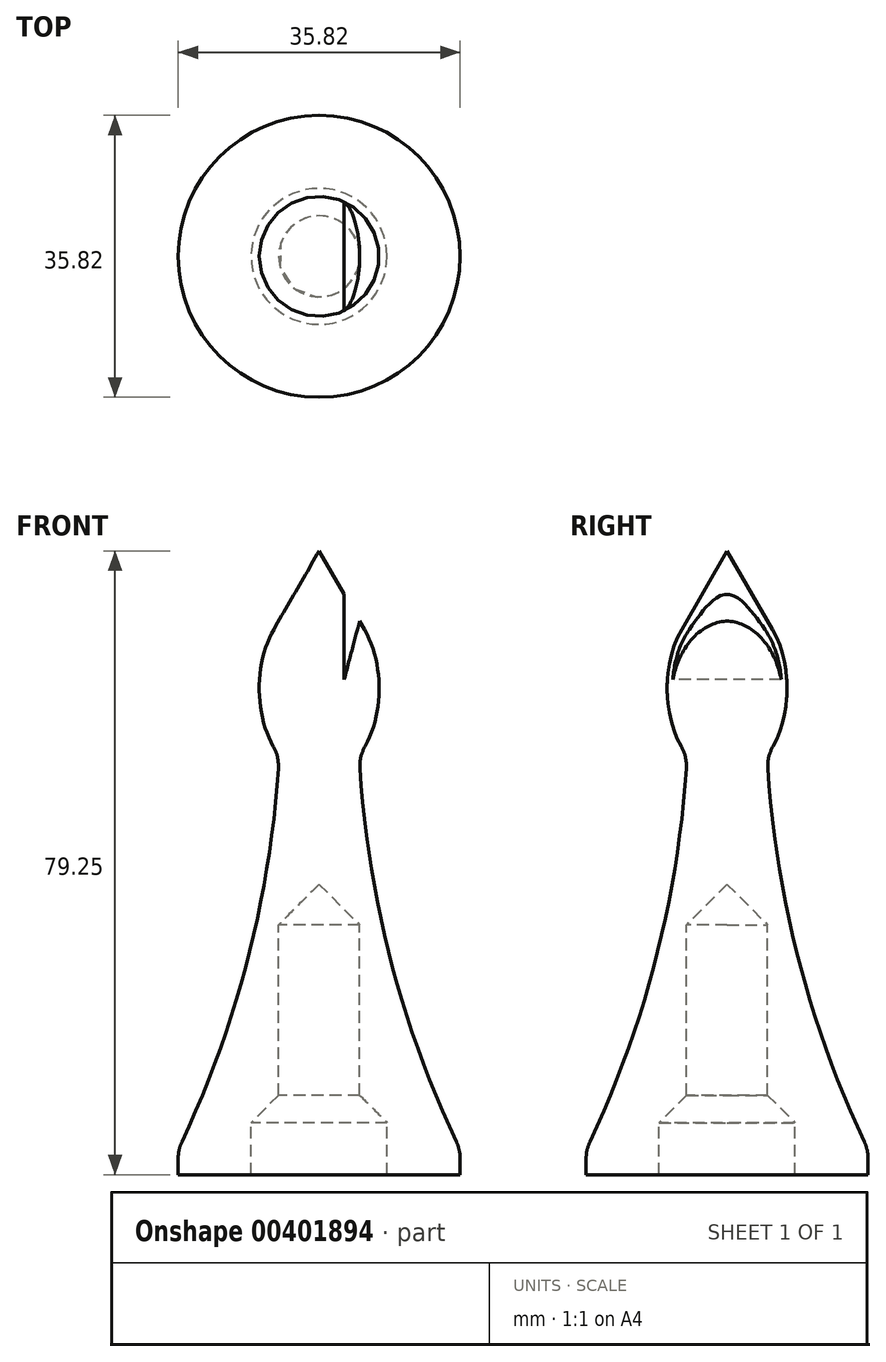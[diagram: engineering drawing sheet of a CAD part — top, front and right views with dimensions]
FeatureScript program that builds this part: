
annotation { "Feature Type Name" : "Feature", "Feature Type Description" : "" }
export const myFeature = defineFeature(function(context is Context, id is Id, definition is map)
    precondition{}
    {
        {
            var Q0;
            Q0=qCreatedBy(makeId("Front.planeOp"),FACE);
            var sketch = newSketch(context, id + "F0", { "sketchPlane" : qUnion([Q0])});
            skLineSegment(sketch, "E0", {"start": v(0, 0) * mm, "end": v(-8.64, 0) * mm, "construction": true});
            skLineSegment(sketch, "E1", {"start": v(-17.9, 0) * mm, "end": v(-17.9, 3.17) * mm});
            skArc(sketch, "E2", {"start": v(-17.9, 3.17) * mm, "mid": v(-9, 27.62) * mm, "end": v(-5.08, 53.34) * mm});
            skLineSegment(sketch, "E3", {"start": v(0, 79.25) * mm, "end": v(0, 36.9) * mm});
            skLineSegment(sketch, "E4", {"start": v(-5.08, 53.34) * mm, "end": v(-3.4, 85.4) * mm, "construction": true});
            skLineSegment(sketch, "E5", {"start": v(-5.76, 69.27) * mm, "end": v(0, 79.25) * mm});
            skEllipticalArc(sketch, "E6", {});
            skLineSegment(sketch, "E7", {"start": v(0, 36.9) * mm, "end": v(-5.14, 31.75) * mm});
            skLineSegment(sketch, "E8", {"start": v(-5.14, 31.75) * mm, "end": v(-5.14, 10.1) * mm});
            skLineSegment(sketch, "E9", {"start": v(-5.14, 10.1) * mm, "end": v(-8.64, 6.6) * mm});
            skLineSegment(sketch, "E10", {"start": v(-8.64, 6.6) * mm, "end": v(-8.64, 0) * mm});
            skLineSegment(sketch, "E11", {"start": v(0, 36.9) * mm, "end": v(0, 0) * mm, "construction": true});
            skLineSegment(sketch, "E12", {"start": v(-8.64, 0) * mm, "end": v(-17.9, 0) * mm});
            const initialGuessF0  = {"E6": [0, 0.06178838660221825, 0, 1, 0.01143, 0.00762, 0.8570719478501309, 2.411249708736111]};
            skSetInitialGuess(sketch, initialGuessF0);
            skSolve(sketch);
        }
        {
            var Q0;
            {var subQ1=sQuery(id+"F0.wireOp",EDGE,"E1");Q0=makeQuery(id+"F0.imprint","IMPRINT",FACE,{"disambiguationData":[TD([[makeQuery(id+"F0.imprint","IMPRINT",EDGE,{"derivedFrom":subQ1}),-1.0]])]});}
            var Q1;
            Q1=sQuery(id+"F0.wireOp",EDGE,"E11");
            revolve(context, id + "F1", {"entities" : qUnion([Q0]), "axis" : qUnion([Q1]), "revolveType" : RevolveType.FULL});
        }
        {
            var Q0;
            Q0=qCreatedBy(makeId("Front.planeOp"),FACE);
            var sketch = newSketch(context, id + "F2", { "sketchPlane" : qUnion([Q0])});
            skLineSegment(sketch, "E13", {"start": v(3.17, 79.01) * mm, "end": v(3.17, 62.92) * mm});
            skLineSegment(sketch, "E14", {"start": v(3.17, 62.92) * mm, "end": v(7.28, 78.25) * mm});
            skLineSegment(sketch, "E15", {"start": v(7.28, 78.25) * mm, "end": v(3.17, 79.01) * mm});
            skSolve(sketch);
        }
        {
            var Q0;
            Q0 = qSketchRegion(id + "F2", true);
            extrude(context, id + "F3", {"entities" : qUnion([Q0]), "operationType" : NewBodyOperationType.REMOVE, "oppositeDirection" : true, "depth" : 25.4 * mm, "symmetric" : true});
        }
        {
            var Q0;
            Q0=makeQuery(id+"F1.opRevolve","SWEPT_EDGE",EDGE,{"disambiguationData":[OSD([sQuery(id+"F0.wireOp",EDGE,"E2"),sQuery(id+"F0.wireOp",EDGE,"TYr9lhgq-TRWa-YIgd-hTFC-wK3aNsaVSOy6")])]});
            fillet(context, id + "F4", {"entities" : qUnion([Q0]), "radius" : 5.08 * mm, "tangentPropagation" : true, "allowEdgeOverflow" : false});
        }
    });
